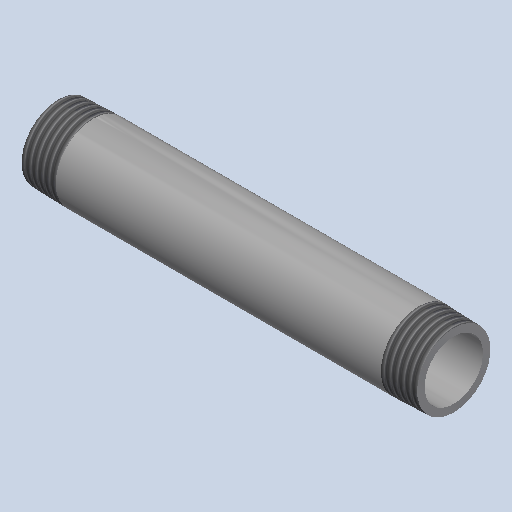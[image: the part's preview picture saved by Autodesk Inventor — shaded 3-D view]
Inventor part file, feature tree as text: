
AUTODESK INVENTOR PART (.ipt)
format: ipt  version: 2025 (Build 290162000, 162)  size: 195,072 bytes
history: native  units: mm (DEFAULTED — no unit token found)
features: other x8, revolve x1
ambient origin geometry x8: Origin, YZ Plane, XZ Plane, XY Plane, X Axis, Y Axis, Z Axis, Center Point
bodies: Solid1 (feature_tree)
feature tree (9):
  revolve  "Revolution1"  [1 undecoded]
  other  "Work Axis1"
  other  "Work Point5"
  other  "Work Axis2"
  other  "Work Point6"
  other  "Work Axis3"
  other  "Work Axis4"
  other  "Work Point7"
  other  "Work Point8"
note: 1 required parameter value undecoded (feature->parameter linkage not recoverable at this tier; creation-order binding heuristic only, values carry confidence <= 0.55)
